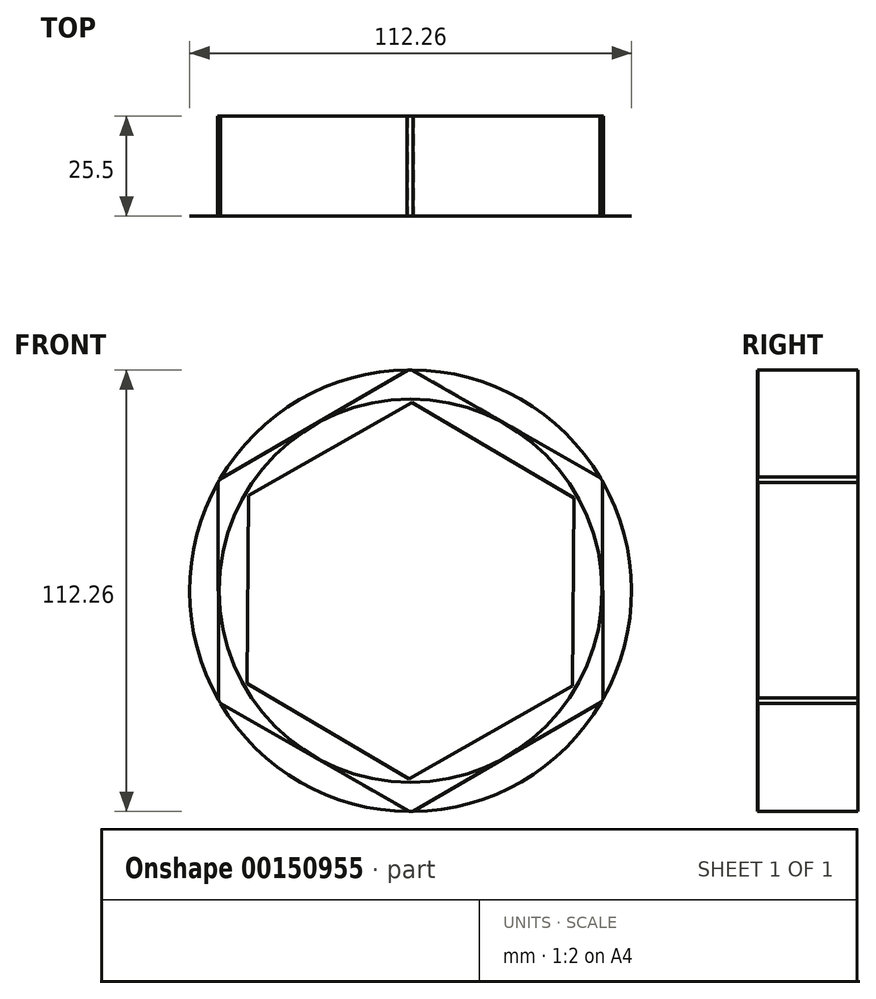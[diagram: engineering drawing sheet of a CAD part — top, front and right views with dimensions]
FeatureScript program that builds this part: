
annotation { "Feature Type Name" : "Feature", "Feature Type Description" : "" }
export const myFeature = defineFeature(function(context is Context, id is Id, definition is map)
    precondition{}
    {
        {
            var Q0;
            Q0=qCreatedBy(makeId("Front.planeOp"),FACE);
            var sketch = newSketch(context, id + "F0", { "sketchPlane" : qUnion([Q0])});
            skCircle(sketch, "E0", {"center": v(0, 0) * mm, "radius": 56.13 * mm});
            skSolve(sketch);
        }
        {
            var Q0;
            Q0=makeQuery(id+"F0.imprint","IMPRINT",FACE,{"disambiguationData":[TD([[makeQuery(id+"F0.imprint","IMPRINT",EDGE,{"derivedFrom":sQuery(id+"F0.wireOp",EDGE,"E0")}),1.0]])]});
            extrude(context, id + "F1", {"entities" : qUnion([Q0]), "depth" : 0.03 * mm});
        }
        {
            var Q0;
            Q0=makeQuery(id+"F1.opExtrude","CAP_FACE",FACE,{"disambiguationData":[OSD([sQuery(id+"F0.wireOp",EDGE,"E0")])],"isStart":false});
            var sketch = newSketch(context, id + "F2", { "sketchPlane" : qUnion([Q0])});
            skCircle(sketch, "E1.cCircle", {"center": v(0, 0) * mm, "radius": 48.83 * mm, "construction": true});
            skLineSegment(sketch, "E1.0", {"start": v(-0.16, 56.38) * mm, "end": v(48.75, 28.33) * mm});
            skLineSegment(sketch, "E1.1", {"start": v(48.75, 28.33) * mm, "end": v(48.91, -28.05) * mm});
            skLineSegment(sketch, "E1.2", {"start": v(48.91, -28.05) * mm, "end": v(0.16, -56.38) * mm});
            skLineSegment(sketch, "E1.3", {"start": v(0.16, -56.38) * mm, "end": v(-48.75, -28.33) * mm});
            skLineSegment(sketch, "E1.4", {"start": v(-48.75, -28.33) * mm, "end": v(-48.91, 28.05) * mm});
            skLineSegment(sketch, "E1.5", {"start": v(-48.91, 28.05) * mm, "end": v(-0.16, 56.38) * mm});
            skPoint(sketch, "E1.0.midPoint", {"position": v(24.3, 42.36) * mm});
            skSolve(sketch);
        }
        {
            var Q0;
            {var subQ1=makeQuery(id+"F1.opExtrude","CAP_EDGE",EDGE,{"disambiguationData":[OSD([sQuery(id+"F0.wireOp",EDGE,"E0")])],"isStart":false});var subQ6=sQuery(id+"F2.wireOp",EDGE,"E1.0");var subQ10=makeQuery(id+"F2.imprint","INTERSECT",VERTEX,{"disambiguationData":[OD(0.0)],"derivedFrom":[subQ1,subQ6]});Q0=makeQuery(id+"F2.imprint","IMPRINT",FACE,{"disambiguationData":[TD([[makeQuery(id+"F2.imprint","IMPRINT",EDGE,{"disambiguationData":[TD([[subQ10,-1.0]])],"derivedFrom":subQ6}),-1.0]])]});}
            extrude(context, id + "F3", {"entities" : qUnion([Q0]), "operationType" : NewBodyOperationType.ADD, "depth" : 0.03 * mm});
        }
        {
            var Q0;
            Q0=makeQuery(id+"F3.opExtrude","CAP_FACE",FACE,{"disambiguationData":[OSD([sQuery(id+"F0.wireOp",EDGE,"E0"),sQuery(id+"F2.wireOp",EDGE,"E1.0"),sQuery(id+"F2.wireOp",EDGE,"E1.1"),sQuery(id+"F2.wireOp",EDGE,"E1.2"),sQuery(id+"F2.wireOp",EDGE,"E1.3"),sQuery(id+"F2.wireOp",EDGE,"E1.4"),sQuery(id+"F2.wireOp",EDGE,"E1.5")])],"isStart":false});
            var sketch = newSketch(context, id + "F4", { "sketchPlane" : qUnion([Q0])});
            skCircle(sketch, "E2", {"center": v(0, 0) * mm, "radius": 48.68 * mm});
            skSolve(sketch);
        }
        {
            var Q0;
            Q0=makeQuery(id+"F4.imprint","IMPRINT",FACE,{"disambiguationData":[TD([[makeQuery(id+"F4.imprint","IMPRINT",EDGE,{"derivedFrom":sQuery(id+"F4.wireOp",EDGE,"E2")}),1.0]])]});
            extrude(context, id + "F5", {"entities" : qUnion([Q0]), "operationType" : NewBodyOperationType.ADD, "depth" : 0.03 * mm});
        }
        {
            var Q0;
            Q0=makeQuery(id+"F5.opExtrude","CAP_FACE",FACE,{"disambiguationData":[OSD([sQuery(id+"F4.wireOp",EDGE,"E2")])],"isStart":false});
            var sketch = newSketch(context, id + "F6", { "sketchPlane" : qUnion([Q0])});
            skCircle(sketch, "E3.cCircle", {"center": v(0, 0) * mm, "radius": 41.37 * mm, "construction": true});
            skLineSegment(sketch, "E3.0", {"start": v(0.35, 47.77) * mm, "end": v(41.55, 23.58) * mm});
            skLineSegment(sketch, "E3.1", {"start": v(41.55, 23.58) * mm, "end": v(41.2, -24.2) * mm});
            skLineSegment(sketch, "E3.2", {"start": v(41.2, -24.2) * mm, "end": v(-0.35, -47.77) * mm});
            skLineSegment(sketch, "E3.3", {"start": v(-0.35, -47.77) * mm, "end": v(-41.55, -23.58) * mm});
            skLineSegment(sketch, "E3.4", {"start": v(-41.55, -23.58) * mm, "end": v(-41.2, 24.2) * mm});
            skLineSegment(sketch, "E3.5", {"start": v(-41.2, 24.2) * mm, "end": v(0.35, 47.77) * mm});
            skPoint(sketch, "E3.0.midPoint", {"position": v(20.95, 35.68) * mm});
            skSolve(sketch);
        }
        {
            var Q0;
            Q0=makeQuery(id+"F6.imprint","IMPRINT",FACE,{"disambiguationData":[TD([[makeQuery(id+"F6.imprint","IMPRINT",EDGE,{"derivedFrom":sQuery(id+"F6.wireOp",EDGE,"E3.0")}),-1.0]])]});
            extrude(context, id + "F7", {"entities" : qUnion([Q0]), "operationType" : NewBodyOperationType.ADD, "depth" : 0.03 * mm});
        }
        {
            var Q0;
            Q0=makeQuery(id+"F1.opExtrude","CAP_FACE",FACE,{"disambiguationData":[OSD([sQuery(id+"F0.wireOp",EDGE,"E0")])],"isStart":true});
            var sketch = newSketch(context, id + "F8", { "sketchPlane" : qUnion([Q0])});
            skCircle(sketch, "E4.cCircle", {"center": v(0, 0) * mm, "radius": 48.98 * mm, "construction": true});
            skLineSegment(sketch, "E4.0", {"start": v(0.14, 56.56) * mm, "end": v(49.05, 28.16) * mm});
            skLineSegment(sketch, "E4.1", {"start": v(49.05, 28.16) * mm, "end": v(48.91, -28.4) * mm});
            skLineSegment(sketch, "E4.2", {"start": v(48.91, -28.4) * mm, "end": v(-0.14, -56.56) * mm});
            skLineSegment(sketch, "E4.3", {"start": v(-0.14, -56.56) * mm, "end": v(-49.05, -28.16) * mm});
            skLineSegment(sketch, "E4.4", {"start": v(-49.05, -28.16) * mm, "end": v(-48.91, 28.4) * mm});
            skLineSegment(sketch, "E4.5", {"start": v(-48.91, 28.4) * mm, "end": v(0.14, 56.56) * mm});
            skPoint(sketch, "E4.0.midPoint", {"position": v(24.6, 42.36) * mm});
            skSolve(sketch);
        }
        {
            var Q0;
            {var subQ1=makeQuery(id+"F1.opExtrude","CAP_EDGE",EDGE,{"disambiguationData":[OSD([sQuery(id+"F0.wireOp",EDGE,"E0")])],"isStart":true});var subQ14=sQuery(id+"F8.wireOp",EDGE,"E4.0");var subQ18=makeQuery(id+"F8.imprint","INTERSECT",VERTEX,{"disambiguationData":[OD(0.0)],"derivedFrom":[subQ1,subQ14]});Q0=makeQuery(id+"F8.imprint","IMPRINT",FACE,{"disambiguationData":[TD([[makeQuery(id+"F8.imprint","IMPRINT",EDGE,{"disambiguationData":[TD([[subQ18,-1.0]])],"derivedFrom":subQ14}),-1.0]])]});}
            extrude(context, id + "F9", {"entities" : qUnion([Q0]), "operationType" : NewBodyOperationType.ADD, "depth" : 25.4 * mm});
        }
    });
